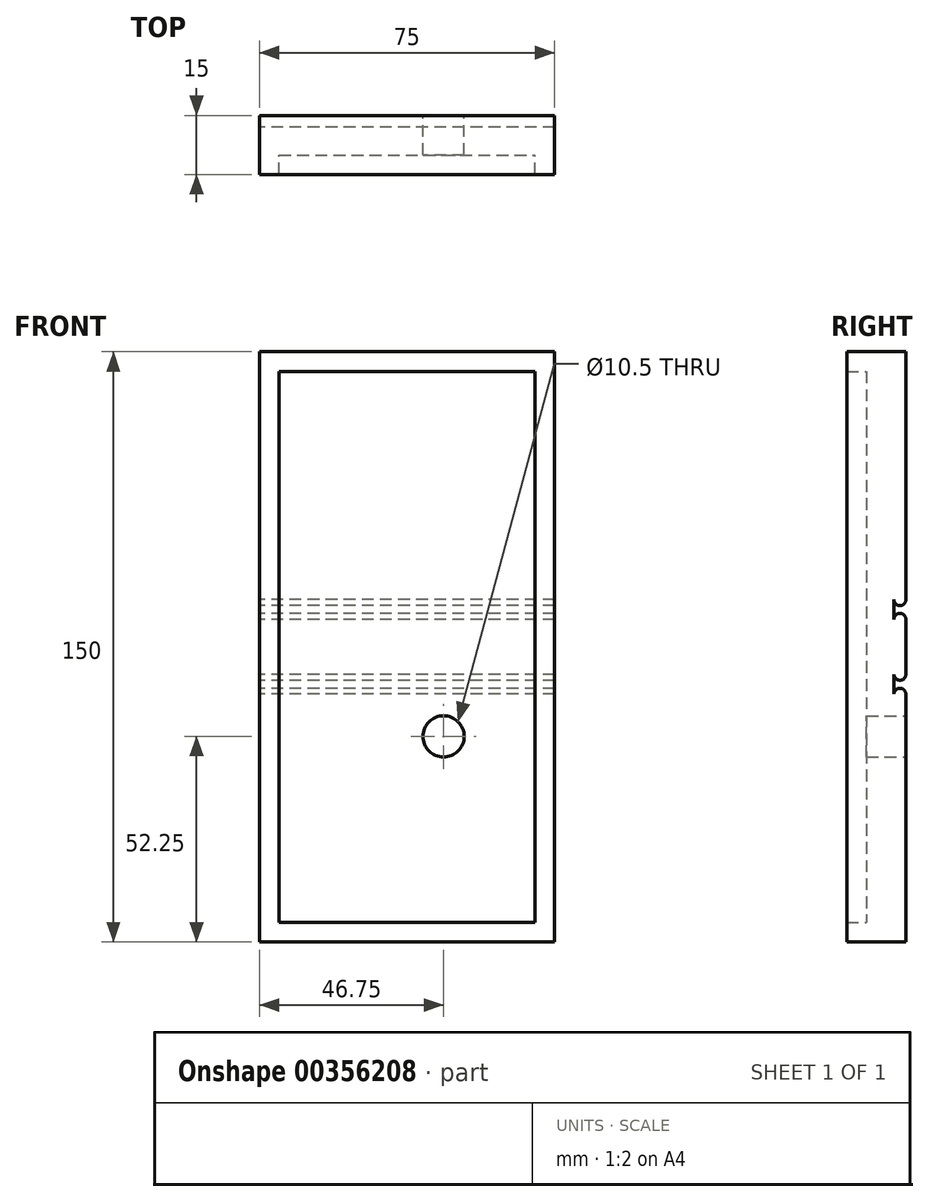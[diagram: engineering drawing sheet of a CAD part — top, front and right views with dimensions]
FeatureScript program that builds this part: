
annotation { "Feature Type Name" : "Feature", "Feature Type Description" : "" }
export const myFeature = defineFeature(function(context is Context, id is Id, definition is map)
    precondition{}
    {
        {
            var Q0;
            Q0=qCreatedBy(makeId("Front.planeOp"),FACE);
            var sketch = newSketch(context, id + "F0", { "sketchPlane" : qUnion([Q0])});
            skCircle(sketch, "E0", {"center": v(9.25, -22.75) * mm, "radius": 5.25 * mm});
            skLineSegment(sketch, "E1.bottom", {"start": v(-37.5, 75) * mm, "end": v(37.5, 75) * mm});
            skLineSegment(sketch, "E1.top", {"start": v(-37.5, -75) * mm, "end": v(37.5, -75) * mm});
            skLineSegment(sketch, "E1.left", {"start": v(-37.5, 75) * mm, "end": v(-37.5, -75) * mm});
            skLineSegment(sketch, "E1.right", {"start": v(37.5, 75) * mm, "end": v(37.5, -75) * mm});
            skLineSegment(sketch, "E2.0", {"start": v(-32.5, 70) * mm, "end": v(32.5, 70) * mm});
            skLineSegment(sketch, "E2.1", {"start": v(-32.5, 70) * mm, "end": v(-32.5, -70) * mm});
            skLineSegment(sketch, "E2.2", {"start": v(-32.5, -70) * mm, "end": v(32.5, -70) * mm});
            skLineSegment(sketch, "E2.3", {"start": v(32.5, 70) * mm, "end": v(32.5, -70) * mm});
            skSolve(sketch);
        }
        {
            var Q0;
            Q0=makeQuery(id+"F0.imprint","IMPRINT",FACE,{"disambiguationData":[TD([[makeQuery(id+"F0.imprint","IMPRINT",EDGE,{"derivedFrom":sQuery(id+"F0.wireOp",EDGE,"E1.bottom")}),-1.0]])]});
            extrude(context, id + "F1", {"entities" : qUnion([Q0]), "depth" : 15 * mm});
        }
        {
            var Q0;
            Q0=makeQuery(id+"F0.imprint","IMPRINT",FACE,{"disambiguationData":[TD([[makeQuery(id+"F0.imprint","IMPRINT",EDGE,{"derivedFrom":sQuery(id+"F0.wireOp",EDGE,"E0")}),-1.0]])]});
            extrude(context, id + "F2", {"entities" : qUnion([Q0]), "operationType" : NewBodyOperationType.ADD, "depth" : 10 * mm});
        }
        {
            var Q0;
            Q0=qCreatedBy(makeId("Right.planeOp"),FACE);
            var sketch = newSketch(context, id + "F3", { "sketchPlane" : qUnion([Q0])});
            skLineSegment(sketch, "E3.bottom", {"start": v(-164.25, 5) * mm, "end": v(-90.25, 5) * mm});
            skLineSegment(sketch, "E3.top", {"start": v(-164.25, 0) * mm, "end": v(-90.25, 0) * mm});
            skLineSegment(sketch, "E3.left", {"start": v(-164.25, 5) * mm, "end": v(-164.25, 0) * mm});
            skLineSegment(sketch, "E3.right", {"start": v(-90.25, 5) * mm, "end": v(-90.25, 0) * mm});
            skLineSegment(sketch, "E4.bottom", {"start": v(-165.54, -13.66) * mm, "end": v(-91.54, -13.66) * mm});
            skLineSegment(sketch, "E4.top", {"start": v(-165.54, -18.66) * mm, "end": v(-91.54, -18.66) * mm});
            skLineSegment(sketch, "E4.left", {"start": v(-165.54, -13.66) * mm, "end": v(-165.54, -18.66) * mm});
            skLineSegment(sketch, "E4.right", {"start": v(-91.54, -13.66) * mm, "end": v(-91.54, -18.66) * mm});
            skLineSegment(sketch, "E5", {"start": v(0, -7) * mm, "end": v(0, -12) * mm});
            skLineSegment(sketch, "E6", {"start": v(-3, -12) * mm, "end": v(-3, -7) * mm});
            skArc(sketch, "E7", {"start": v(0, -12) * mm, "mid": v(-1.5, -10.5) * mm, "end": v(-3, -12) * mm});
            skArc(sketch, "E8", {"start": v(-3, -7) * mm, "mid": v(-1.5, -8.5) * mm, "end": v(0, -7) * mm});
            skLineSegment(sketch, "E9.MirrorCS", {"start": v(-3, 12) * mm, "end": v(-3, 7) * mm});
            skArc(sketch, "E10.MirrorCS", {"start": v(0, 12) * mm, "mid": v(-1.5, 10.5) * mm, "end": v(-3, 12) * mm});
            skArc(sketch, "E11.MirrorCS", {"start": v(-3, 7) * mm, "mid": v(-1.5, 8.5) * mm, "end": v(0, 7) * mm});
            skLineSegment(sketch, "E12", {"start": v(0, 7) * mm, "end": v(0, 12) * mm});
            skSolve(sketch);
        }
        {
            var Q0;
            Q0=makeQuery(id+"F3.imprint","IMPRINT",FACE,{"disambiguationData":[TD([[makeQuery(id+"F3.imprint","IMPRINT",EDGE,{"derivedFrom":sQuery(id+"F3.wireOp",EDGE,"E3.bottom")}),-1.0]])]});
            var Q1;
            Q1=makeQuery(id+"F3.imprint","IMPRINT",FACE,{"disambiguationData":[TD([[makeQuery(id+"F3.imprint","IMPRINT",EDGE,{"derivedFrom":sQuery(id+"F3.wireOp",EDGE,"E4.bottom")}),-1.0]])]});
            extrude(context, id + "F4", {"entities" : qUnion([Q0, Q1]), "depth" : 10 * mm});
        }
        {
            var Q0;
            Q0 = qSketchRegion(id + "F3", true);
            extrude(context, id + "F5", {"entities" : qUnion([Q0]), "operationType" : NewBodyOperationType.REMOVE, "endBound" : BoundingType.THROUGH_ALL, "depth" : 25 * mm, "hasSecondDirection" : true, "secondDirectionBound" : SecondDirectionBoundingType.THROUGH_ALL, "secondDirectionOppositeDirection" : true, "secondDirectionDepth" : 25 * mm});
        }
    });
